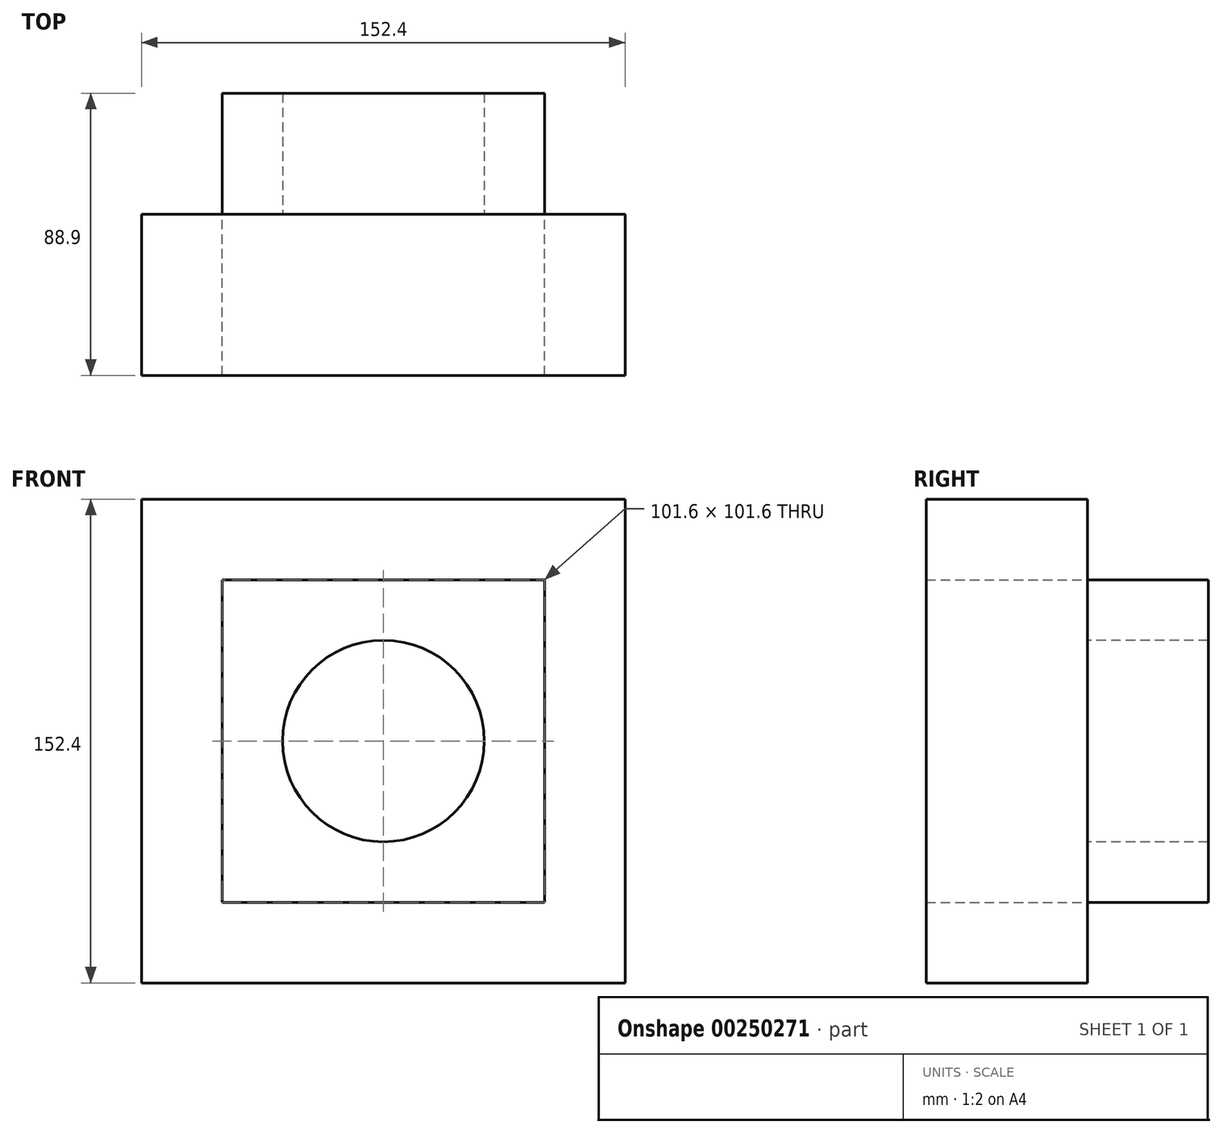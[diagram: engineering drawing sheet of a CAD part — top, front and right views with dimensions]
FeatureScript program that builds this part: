
annotation { "Feature Type Name" : "Feature", "Feature Type Description" : "" }
export const myFeature = defineFeature(function(context is Context, id is Id, definition is map)
    precondition{}
    {
        {
            var Q0;
            Q0=qCreatedBy(makeId("Front.planeOp"),FACE);
            var sketch = newSketch(context, id + "F0", { "sketchPlane" : qUnion([Q0])});
            skCircle(sketch, "E0", {"center": v(0, 0) * mm, "radius": 31.75 * mm});
            skLineSegment(sketch, "E1.bottom", {"start": v(50.8, 50.8) * mm, "end": v(-50.8, 50.8) * mm});
            skLineSegment(sketch, "E1.top", {"start": v(50.8, -50.8) * mm, "end": v(-50.8, -50.8) * mm});
            skLineSegment(sketch, "E1.left", {"start": v(50.8, 50.8) * mm, "end": v(50.8, -50.8) * mm});
            skLineSegment(sketch, "E1.right", {"start": v(-50.8, 50.8) * mm, "end": v(-50.8, -50.8) * mm});
            skLineSegment(sketch, "E2.bottom", {"start": v(76.2, 76.2) * mm, "end": v(-76.2, 76.2) * mm});
            skLineSegment(sketch, "E2.top", {"start": v(76.2, -76.2) * mm, "end": v(-76.2, -76.2) * mm});
            skLineSegment(sketch, "E2.left", {"start": v(76.2, 76.2) * mm, "end": v(76.2, -76.2) * mm});
            skLineSegment(sketch, "E2.right", {"start": v(-76.2, 76.2) * mm, "end": v(-76.2, -76.2) * mm});
            skSolve(sketch);
        }
        {
            var Q0;
            Q0=makeQuery(id+"F0.imprint","IMPRINT",FACE,{"disambiguationData":[TD([[makeQuery(id+"F0.imprint","IMPRINT",EDGE,{"derivedFrom":sQuery(id+"F0.wireOp",EDGE,"E0")}),-1.0]])]});
            extrude(context, id + "F1", {"entities" : qUnion([Q0]), "oppositeDirection" : true, "depth" : 38.1 * mm});
        }
        {
            var Q0;
            Q0=makeQuery(id+"F0.imprint","IMPRINT",FACE,{"disambiguationData":[TD([[makeQuery(id+"F0.imprint","IMPRINT",EDGE,{"derivedFrom":sQuery(id+"F0.wireOp",EDGE,"E1.bottom")}),-1.0]])]});
            extrude(context, id + "F2", {"entities" : qUnion([Q0]), "depth" : 50.8 * mm});
        }
    });
